# Revit family: Siemens_MV_switchgear_gas-insulated_8DA10_40.5kV
name_source: partatom
category: Electrical Fixtures
revit_build: Autodesk Revit 2016 (Build: 20150714_1515(x64)
units: mm (PartAtom-declared; Revit-internal decimal feet)

## family parameters
Always vertical = Yes
Cut with Voids When Loaded = No
Maintain Annotation Orientation = No
OmniClass Number = 23.80.00.00
OmniClass Title = Electric Power and Lighting
Part Type = Normal
Room Calculation Point = No
Round Connector Dimension = Use Diameter
Shared = No
Work Plane-Based = No

## types (6) — shared parameters
Accessory = Lateral switchgear termination
Consultant support for Totally Integrated Power (TIP) = www.siemens.com/tip-cs
Degree of protection = IP 3XD; IP31D; IP41; IP65; IK07
Edition number = 1
IFC Classification = Electric Distribution
Internal arc classification = IAC A FL; IAC A FLR
LST_1 = LST : Lateral switchgear termination left
LST_2 = LST : Lateral switchgear termination right
LST_3 = LST : None
Manufacturer = Siemens AG
Note = Lateral switchgear termination have to be placed at both ends of switchgear rows, not allowed between cubicles
Operating voltage (kV) = 3.3 - 38
Product Guid = e60fa22a-fdec-445f-93e5-cca8522a5483
Product data url = https://bimobject.com
Rated frequency (Hz) = 50;60
Rated lightning impulse withstand voltage (kV) = 75 - 200
Rated normal current busbar (A) = 1250 - 5000
Rated short-duration power-frequency withstand voltage (kV) = 28 - 95
Rated short-time withstand current (kA/s) = 25/3;31.5/3;40/3
Rated voltage (kV) = 4.76 - 40.5
SIMARIS planning tools = www.siemens.com/simaris
Specification texts = www.siemens.com/specifications
Standards = IEC / GOST / GB / UL
Switchgear type = 8DA10
Technical description MV-switchgear = www.siemens.com/medium-voltage-switchgear
Type of arrangement = wall-standing; free-standing
V = 2
V3 = No
V4 = No

## per-type parameters (varying)
- Circuit-breaker panel: 2nd Protection device=without; with (see www.siemens.com/protection); B for Typ=600 mm  [stored 1.9685 ft]; Busbar connection=without; with; with three-position disconnector; Capacitive voltage indicator at busbar and feeder=CAPDIS-S1+; CAPDIS-S2+; LRM; VOIS+; VOIS R+; WEGA 1.2 C; WEGA 1.c Vario; WEGA 2.2 C; WEGA 3; Current transformer at busbar=without; with protection core or/and measuring core; Current transformer at feeder=without; with protection core or/and measuring core; Earthing switch at busbar=without; earthing switch; make-proof earthing switch; Electromechanical interlock=without; Earthing switch; Disconnector; Disconnector and earthing switch; Number of cables (per phase)=1 - 6; Number of operating cycle=2000/1000/-; Panel conection=with inside-cone plug; bar connection; Panel type=LS; Protection device=with (further informations: www.siemens.com/protection); Rated normal current feeder (A)=1250A: 2000A; 2500A; 2750A; 3150A; Surge arrester=without;with; Three-position switch=manual operated; motor operated; Top mounted bus sectionalizer=without; with; Voltage transformer at busbar=without; with; with three-position switch; Voltage transformer at feeder=without; directly plugged-in; plugged-in with cable connection; Zero-sequence current transformer=without; with
- Bus sectionalizer longtudinal: 1st electromechanical interlock=without; Earthing switch; Disconnector; Disconnector and earthing switch; 2nd electromechanical interlock=without; Earthing switch; Disconnector; Disconnector and earthing switch; 2nd three-position switch=manual operated; motor operated; B for Typ=1200 mm  [stored 3.93701 ft]; Busbar connection, left panel=without; with; with three-position disconnector; Busbar connection, right panel=without; with; with three-position disconnector; Capacitive voltage indicator at busbar, left panel=without; CAPDIS-S1+; CAPDIS-S2+; LRM; VOIS+; VOIS R+; WEGA 1.2 C; WEGA 1.c Vario; WEGA 2.2 C; WEGA 3; Capacitive voltage indicator at busbar, right panel=without; CAPDIS-S1+; CAPDIS-S2+; LRM; VOIS+; VOIS R+; WEGA 1.2 C; WEGA 1.c Vario; WEGA 2.2 C; WEGA 3; Capacitive voltage indicator at circuit breaker=same panel as circuit breaker: CAPDIS-S1+; CAPDIS-S2+; LRM; VOIS+; VOIS R+; WEGA 1.2 C; WEGA 1.c Vario; WEGA 2.2 C; WEGA 3; Current transformer at busbar=without; same panel as circuit breaker and with protection core or/and measuring core; Current transformer at busbar, right panel=without; with protection core; Earthing switch at busbar, left panel=without; earthing switch; make-proof earthing switch; Earthing switch at busbar, right panel=without; earthing switch; make-proof earthing switch; Number of operating cycle=at rated normal current: 10000; optional 30000 / at rated short-cicuit breaking current: 50; Panel type=LK; Protection device=with (further informations: www.siemens.com/protection); Rated normal current feeder (A)=1250A: 2000A; 2500A; 2750A; 3150A; Release combination=1f (-Y1); 2f (-Y1, -Y2); 1f (-Y1) + 1r (-Y7); 2f- (-Y1, -Y2) + 1r (-Y7); Three-position switch=manual operated; motor operated; Vacuum circuit breaker=right panel; left panel; Voltage transformer busbar, left panel=without; with; with three-position switch; Voltage transformer busbar, right panel=without; with; with three-position switch
- Metering panel: B for Typ=600 mm  [stored 1.9685 ft]; Capacitive voltage indicator at busbar=without; CAPDIS-S1+; CAPDIS-S2+; LRM; VOIS+; VOIS R+; WEGA 1.2 C; WEGA 1.c Vario; WEGA 2.2 C; WEGA 3; Current transformer at busbar=without; with protection core or/and measuring core; Earthing switch at busbar=without; earthing switch; make-proof earthing switch; Panel type=ME; Three-position switch=manual operated; motor operated; Voltage transformer at busbar=without; with; with three-position switch; Voltage transformer at feeder=without; 3 x single-pole; 3 x single-pole with earth-fault winding and damping resistor
- Cable connection panel: B for Typ=600 mm  [stored 1.9685 ft]; Capacitive voltage indicator at feeder=CAPDIS-S1+; CAPDIS-S2+; LRM; VOIS+; VOIS R+; WEGA 1.2 C; WEGA 1.c Vario; WEGA 2.2 C; WEGA 3; Current transformer at busbar=without; with protection core or/and measuring core; Number of cables (per phase)=1 - 6; Panel conection=cable with inside-cone plug; bar connection; Panel type=CC; Rated normal current feeder (A)=1250; 2000; 2500; 2750; 3150; Three-position switch=manual operated; motor operated
- Empty panel: B for Typ=600 mm  [stored 1.9685 ft]; Panel type=EP
- Disconnector panel: 2nd Protection device=without; with (see www.siemens.com/protection); B for Typ=600 mm  [stored 1.9685 ft]; Busbar connection=without; with; with three-position disconnector; Capacitive voltage indicator at busbar and feeder=CAPDIS-S1+; CAPDIS-S2+; LRM; VOIS+; VOIS R+; WEGA 1.2 C; WEGA 1.c Vario; WEGA 2.2 C; WEGA 3; Current transformer at busbar=without; with protection core or/and measuring core; Current transformer at feeder=without; with protection core or/and measuring core; Earthing switch at busbar=without; earthing switch; make-proof earthing switch; Electromechanical interlock=without; Earthing switch; Disconnector; Disconnector and earthing switch; Number of cables (per phase)=1 - 6; Number of operating cycle=2000/1000/-; Panel conection=with inside-cone plug; bar connection; Panel type=TS; Protection device=with (further informations: www.siemens.com/protection); Rated normal current feeder (A)=1250A: 2000A; 2500A; 2750A; 3150A; Surge arrester=without;with; Three-position switch=manual operated; motor operated; Top mounted bus sectionalizer=without; with; Voltage transformer at busbar=without; with; with three-position switch; Voltage transformer at feeder=without; directly plugged-in; plugged-in with cable connection; Zero-sequence current transformer=without; with

note: column(s) folded — value = type name in every type: Model

note: [stored X ft] marks values corroborated as IEEE doubles in the binary element streams (Revit-internal decimal feet)

## geometry (parser evidence)
native form markers: Blend x9, Sweep x2
no freeform markers — native parametric forms only
